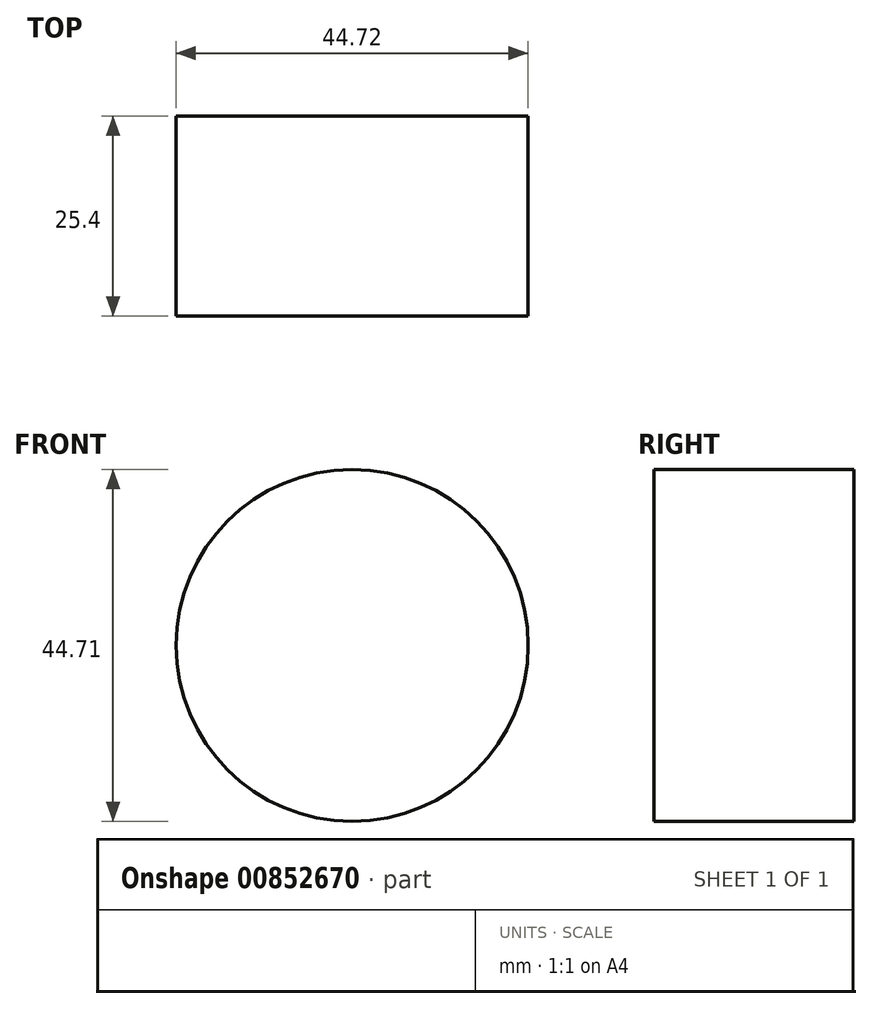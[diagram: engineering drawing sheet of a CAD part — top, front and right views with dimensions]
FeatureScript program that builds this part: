
annotation { "Feature Type Name" : "Feature", "Feature Type Description" : "" }
export const myFeature = defineFeature(function(context is Context, id is Id, definition is map)
    precondition{}
    {
        {
            var Q0;
            Q0=qCreatedBy(makeId("Front.planeOp"),FACE);
            var sketch = newSketch(context, id + "F0", { "sketchPlane" : qUnion([Q0])});
            skLineSegment(sketch, "E0", {"start": v(-36.23, 42.86) * mm, "end": v(37.88, 42.86) * mm});
            skLineSegment(sketch, "E1", {"start": v(37.88, 42.86) * mm, "end": v(37.88, -45.44) * mm});
            skLineSegment(sketch, "E2", {"start": v(37.88, -45.44) * mm, "end": v(-40.47, -45.44) * mm});
            skLineSegment(sketch, "E3", {"start": v(-40.47, -45.44) * mm, "end": v(-36.23, 42.86) * mm});
            skCircle(sketch, "E4", {"center": v(0, -1.57) * mm, "radius": 22.36 * mm});
            skSolve(sketch);
        }
        {
            var Q0;
            Q0=makeQuery(id+"F0.imprint","IMPRINT",FACE,{"disambiguationData":[TD([[makeQuery(id+"F0.imprint","IMPRINT",EDGE,{"derivedFrom":sQuery(id+"F0.wireOp",EDGE,"E4")}),1.0]])]});
            extrude(context, id + "F1", {"entities" : qUnion([Q0]), "depth" : 25.4 * mm, "offsetDistance" : 25.4 * mm});
        }
    });
